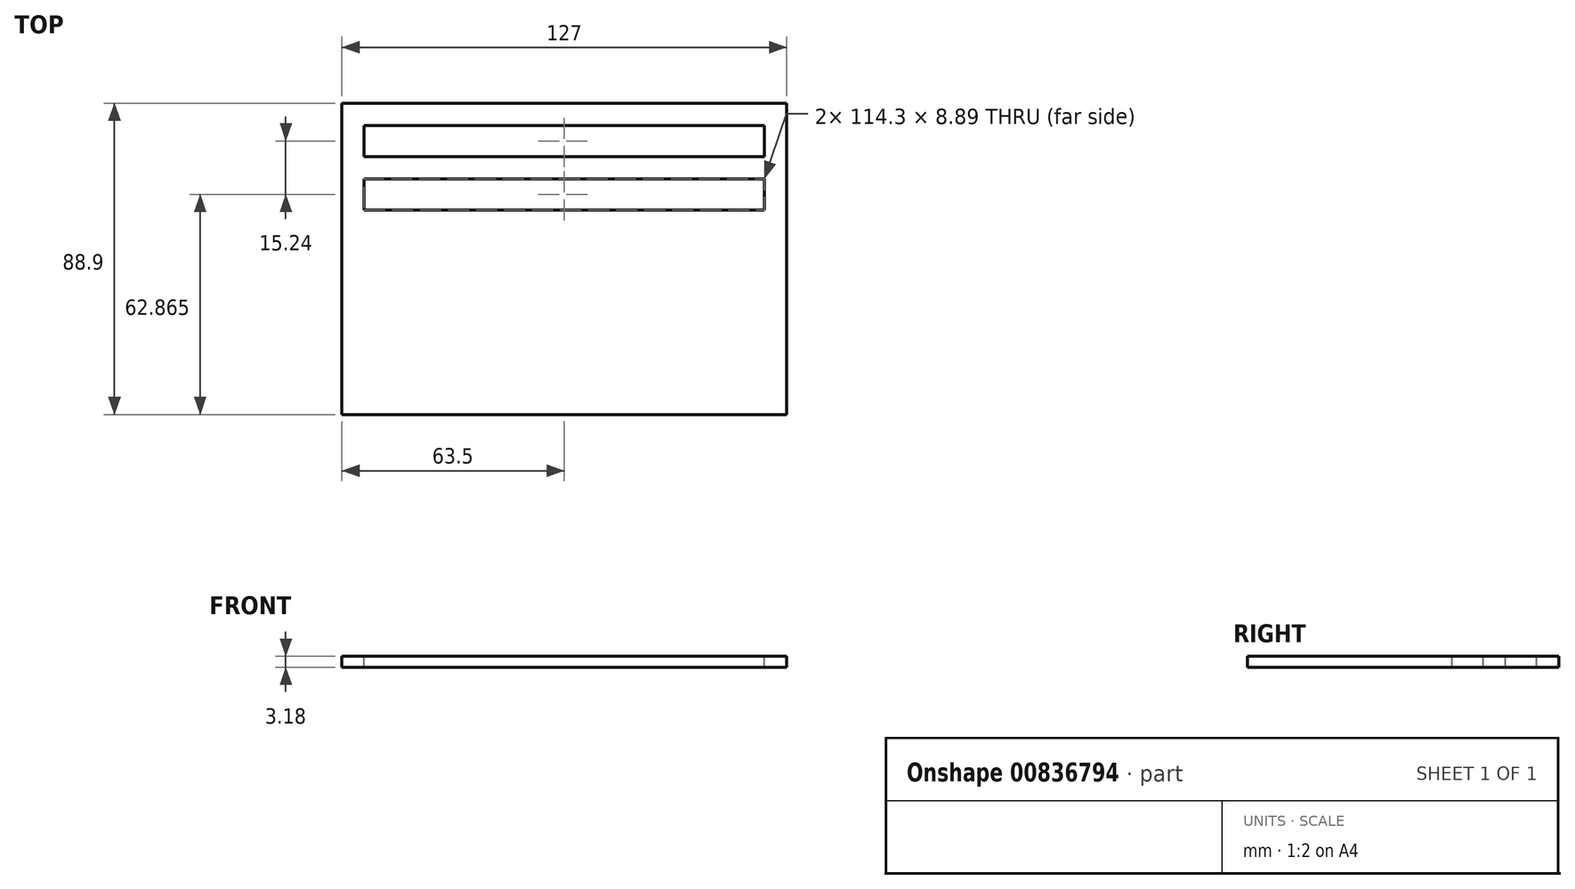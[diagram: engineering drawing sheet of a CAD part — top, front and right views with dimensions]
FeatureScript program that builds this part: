
annotation { "Feature Type Name" : "Feature", "Feature Type Description" : "" }
export const myFeature = defineFeature(function(context is Context, id is Id, definition is map)
    precondition{}
    {
        {
            var Q0;
            Q0=qCreatedBy(makeId("Top.planeOp"),FACE);
            var sketch = newSketch(context, id + "F0", { "sketchPlane" : qUnion([Q0])});
            skLineSegment(sketch, "E0.bottom", {"start": v(-63.5, 25.4) * mm, "end": v(63.5, 25.4) * mm});
            skLineSegment(sketch, "E0.top", {"start": v(-63.5, -63.5) * mm, "end": v(63.5, -63.5) * mm});
            skLineSegment(sketch, "E0.left", {"start": v(-63.5, 25.4) * mm, "end": v(-63.5, -63.5) * mm});
            skLineSegment(sketch, "E0.right", {"start": v(63.5, 25.4) * mm, "end": v(63.5, -63.5) * mm});
            skSolve(sketch);
        }
        {
            var Q0;
            Q0 = qSketchRegion(id + "F0", true);
            extrude(context, id + "F1", {"entities" : qUnion([Q0]), "depth" : 3.17 * mm, "offsetDistance" : 25.4 * mm});
        }
        {
            var Q0;
            Q0=makeQuery(id+"F1.opExtrude","CAP_FACE",FACE,{"disambiguationData":[OSD([sQuery(id+"F0.wireOp",EDGE,"E0.bottom"),sQuery(id+"F0.wireOp",EDGE,"E0.top"),sQuery(id+"F0.wireOp",EDGE,"E0.left"),sQuery(id+"F0.wireOp",EDGE,"E0.right")])],"isStart":false});
            var sketch = newSketch(context, id + "F2", { "sketchPlane" : qUnion([Q0])});
            skLineSegment(sketch, "E1.bottom", {"start": v(-57.15, 19.05) * mm, "end": v(57.15, 19.05) * mm});
            skLineSegment(sketch, "E1.top", {"start": v(-57.15, 10.16) * mm, "end": v(57.15, 10.16) * mm});
            skLineSegment(sketch, "E1.left", {"start": v(-57.15, 19.05) * mm, "end": v(-57.15, 10.16) * mm});
            skLineSegment(sketch, "E1.right", {"start": v(57.15, 19.05) * mm, "end": v(57.15, 10.16) * mm});
            skLineSegment(sketch, "E2.bottom", {"start": v(-57.15, 3.8) * mm, "end": v(57.15, 3.8) * mm});
            skLineSegment(sketch, "E2.top", {"start": v(-57.15, -5.08) * mm, "end": v(57.15, -5.08) * mm});
            skLineSegment(sketch, "E2.left", {"start": v(-57.15, 3.8) * mm, "end": v(-57.15, -5.08) * mm});
            skLineSegment(sketch, "E2.right", {"start": v(57.15, 3.8) * mm, "end": v(57.15, -5.08) * mm});
            skSolve(sketch);
        }
        {
            var Q0;
            Q0 = qSketchRegion(id + "F2", true);
            extrude(context, id + "F3", {"entities" : qUnion([Q0]), "operationType" : NewBodyOperationType.REMOVE, "endBound" : BoundingType.THROUGH_ALL, "oppositeDirection" : true, "depth" : 25.4 * mm, "offsetDistance" : 25.4 * mm});
        }
    });
